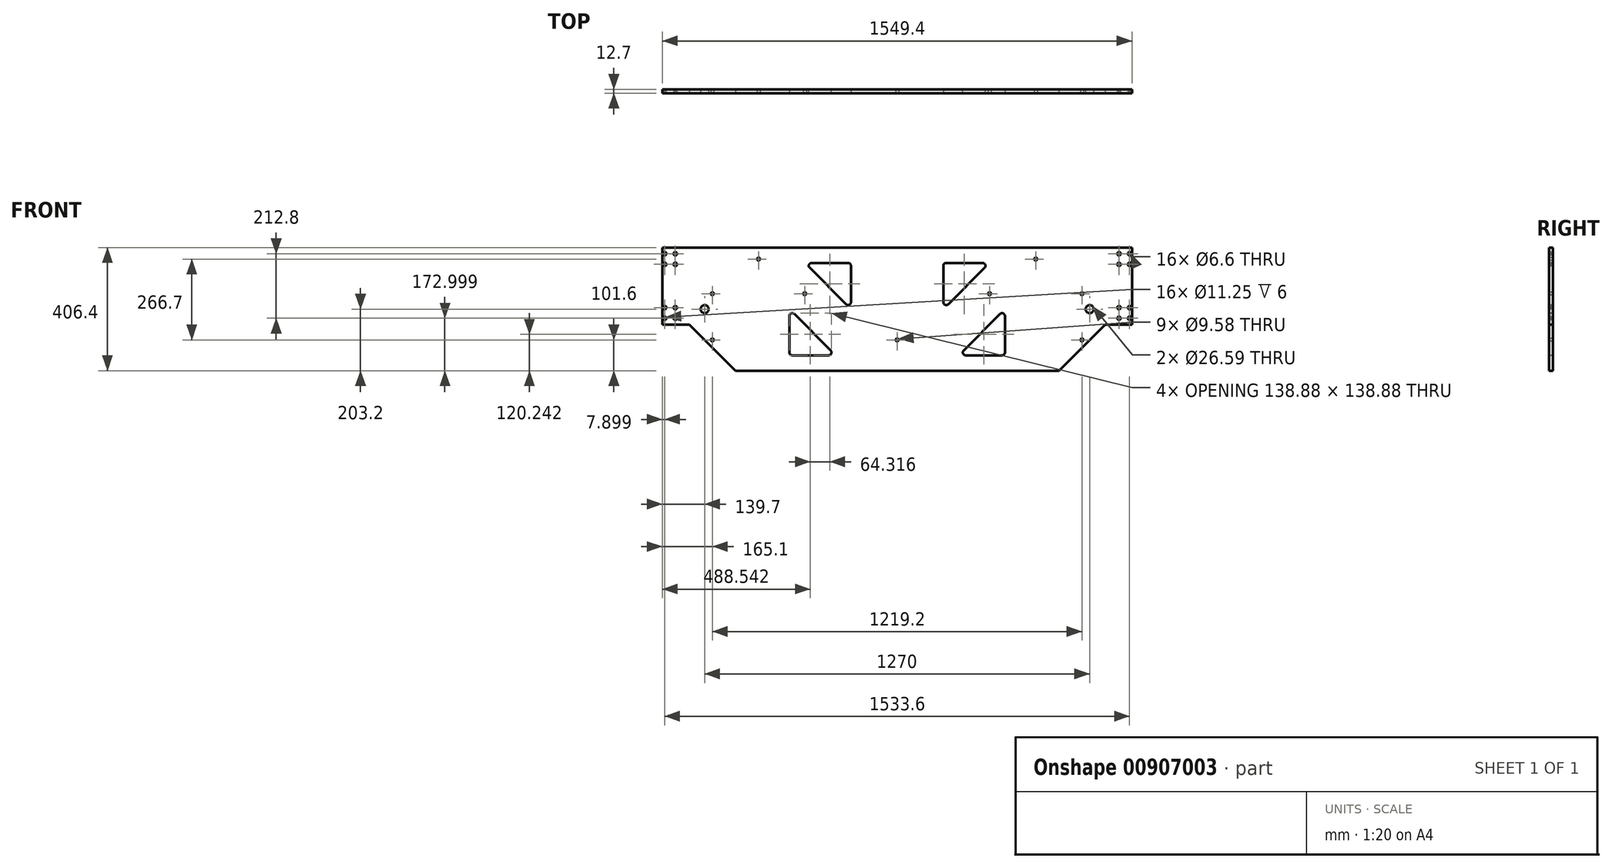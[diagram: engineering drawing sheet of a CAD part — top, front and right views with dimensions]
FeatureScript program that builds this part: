
annotation { "Feature Type Name" : "Feature", "Feature Type Description" : "" }
export const myFeature = defineFeature(function(context is Context, id is Id, definition is map)
    precondition{}
    {
        {
            var Q0;
            Q0=qCreatedBy(makeId("Front.planeOp"),FACE);
            var sketch = newSketch(context, id + "F0", { "sketchPlane" : qUnion([Q0])});
            skLineSegment(sketch, "E0.bottom", {"start": v(774.7, 127) * mm, "end": v(-774.7, 127) * mm});
            skLineSegment(sketch, "E0.top", {"start": v(774.7, -127) * mm, "end": v(-774.7, -127) * mm});
            skLineSegment(sketch, "E0.left", {"start": v(774.7, 127) * mm, "end": v(774.7, -127) * mm});
            skLineSegment(sketch, "E0.right", {"start": v(-774.7, 127) * mm, "end": v(-774.7, -127) * mm});
            skPoint(sketch, "E0.middle", {"position": v(0, 0) * mm});
            skSolve(sketch);
        }
        {
            var Q0;
            Q0=makeQuery(id+"F0.imprint","IMPRINT",FACE,{"disambiguationData":[TD([[makeQuery(id+"F0.imprint","IMPRINT",EDGE,{"derivedFrom":sQuery(id+"F0.wireOp",EDGE,"E0.bottom")}),1.0]])]});
            extrude(context, id + "F1", {"entities" : qUnion([Q0]), "depth" : 12.7 * mm, "offsetDistance" : 25.4 * mm});
        }
        {
            var Q0;
            Q0=makeQuery(id+"F1.opExtrude","CAP_FACE",FACE,{"disambiguationData":[OSD([sQuery(id+"F0.wireOp",EDGE,"E0.bottom"),sQuery(id+"F0.wireOp",EDGE,"E0.top"),sQuery(id+"F0.wireOp",EDGE,"E0.left"),sQuery(id+"F0.wireOp",EDGE,"E0.right")])],"isStart":false});
            var sketch = newSketch(context, id + "F2", { "sketchPlane" : qUnion([Q0])});
            skLineSegment(sketch, "E1.bottom", {"start": v(-766.8, 106.4) * mm, "end": v(-731.8, 106.4) * mm, "construction": true});
            skLineSegment(sketch, "E1.top", {"start": v(-766.8, 71.4) * mm, "end": v(-731.8, 71.4) * mm, "construction": true});
            skLineSegment(sketch, "E1.left", {"start": v(-766.8, 106.4) * mm, "end": v(-766.8, 71.4) * mm, "construction": true});
            skLineSegment(sketch, "E1.right", {"start": v(-731.8, 106.4) * mm, "end": v(-731.8, 71.4) * mm, "construction": true});
            skLineSegment(sketch, "E2.0.1.0", {"start": v(-766.8, -71.4) * mm, "end": v(-766.8, -106.4) * mm, "construction": true});
            skLineSegment(sketch, "E2.0.1.1", {"start": v(-766.8, -71.4) * mm, "end": v(-731.8, -71.4) * mm, "construction": true});
            skLineSegment(sketch, "E2.0.1.2", {"start": v(-766.8, -106.4) * mm, "end": v(-731.8, -106.4) * mm, "construction": true});
            skLineSegment(sketch, "E2.0.1.3", {"start": v(-731.8, -71.4) * mm, "end": v(-731.8, -106.4) * mm, "construction": true});
            skLineSegment(sketch, "E2.1.0.0", {"start": v(731.8, 106.4) * mm, "end": v(731.8, 71.4) * mm, "construction": true});
            skLineSegment(sketch, "E2.1.0.1", {"start": v(731.8, 106.4) * mm, "end": v(766.8, 106.4) * mm, "construction": true});
            skLineSegment(sketch, "E2.1.0.2", {"start": v(731.8, 71.4) * mm, "end": v(766.8, 71.4) * mm, "construction": true});
            skLineSegment(sketch, "E2.1.0.3", {"start": v(766.8, 106.4) * mm, "end": v(766.8, 71.4) * mm, "construction": true});
            skLineSegment(sketch, "E2.1.1.0", {"start": v(731.8, -71.4) * mm, "end": v(731.8, -106.4) * mm, "construction": true});
            skLineSegment(sketch, "E2.1.1.1", {"start": v(731.8, -71.4) * mm, "end": v(766.8, -71.4) * mm, "construction": true});
            skLineSegment(sketch, "E2.1.1.2", {"start": v(731.8, -106.4) * mm, "end": v(766.8, -106.4) * mm, "construction": true});
            skLineSegment(sketch, "E2.1.1.3", {"start": v(766.8, -71.4) * mm, "end": v(766.8, -106.4) * mm, "construction": true});
            skLineSegment(sketch, "E2.2.0.0", {"start": v(2230.4, 106.4) * mm, "end": v(2230.4, 71.4) * mm, "construction": true});
            skLineSegment(sketch, "E2.2.0.1", {"start": v(2230.4, 106.4) * mm, "end": v(2265.4, 106.4) * mm, "construction": true});
            skLineSegment(sketch, "E2.2.0.2", {"start": v(2230.4, 71.4) * mm, "end": v(2265.4, 71.4) * mm, "construction": true});
            skLineSegment(sketch, "E2.2.0.3", {"start": v(2265.4, 106.4) * mm, "end": v(2265.4, 71.4) * mm, "construction": true});
            skLineSegment(sketch, "E2.2.1.0", {"start": v(2230.4, -71.4) * mm, "end": v(2230.4, -106.4) * mm, "construction": true});
            skLineSegment(sketch, "E2.2.1.1", {"start": v(2230.4, -71.4) * mm, "end": v(2265.4, -71.4) * mm, "construction": true});
            skLineSegment(sketch, "E2.2.1.2", {"start": v(2230.4, -106.4) * mm, "end": v(2265.4, -106.4) * mm, "construction": true});
            skLineSegment(sketch, "E2.2.1.3", {"start": v(2265.4, -71.4) * mm, "end": v(2265.4, -106.4) * mm, "construction": true});
            skLineSegment(sketch, "E2.direction1", {"start": v(-766.8, 71.4) * mm, "end": v(731.8, 71.4) * mm, "construction": true});
            skLineSegment(sketch, "E2.direction2", {"start": v(-766.8, 71.4) * mm, "end": v(-766.8, -106.4) * mm, "construction": true});
            skSolve(sketch);
        }
        {
            var Q0;
            Q0=sQuery(id+"F2.wireOp",VERTEX,"E1.bottom.start");
            var Q1;
            Q1=sQuery(id+"F2.wireOp",VERTEX,"E1.bottom.end");
            var Q2;
            Q2=sQuery(id+"F2.wireOp",VERTEX,"E1.top.end");
            var Q3;
            Q3=sQuery(id+"F2.wireOp",VERTEX,"E1.top.start");
            var Q4;
            Q4=sQuery(id+"F2.wireOp",VERTEX,"E2.0.1.1.end");
            var Q5;
            Q5=sQuery(id+"F2.wireOp",VERTEX,"E2.0.1.0.start");
            var Q6;
            Q6=sQuery(id+"F2.wireOp",VERTEX,"E2.0.1.0.end");
            var Q7;
            Q7=sQuery(id+"F2.wireOp",VERTEX,"E2.0.1.2.end");
            var Q8;
            Q8=sQuery(id+"F2.wireOp",VERTEX,"E2.1.0.0.start");
            var Q9;
            Q9=sQuery(id+"F2.wireOp",VERTEX,"E2.1.0.1.end");
            var Q10;
            Q10=sQuery(id+"F2.wireOp",VERTEX,"E2.1.0.2.end");
            var Q11;
            Q11=sQuery(id+"F2.wireOp",VERTEX,"E2.1.0.0.end");
            var Q12;
            Q12=sQuery(id+"F2.wireOp",VERTEX,"E2.1.1.0.start");
            var Q13;
            Q13=sQuery(id+"F2.wireOp",VERTEX,"E2.1.1.1.end");
            var Q14;
            Q14=sQuery(id+"F2.wireOp",VERTEX,"E2.1.1.2.end");
            var Q15;
            Q15=sQuery(id+"F2.wireOp",VERTEX,"E2.1.1.0.end");
            var Q16;
            Q16=makeQuery(id+"F1.opExtrude","SWEPT_BODY",BODY,{"disambiguationData":[OSD([sQuery(id+"F0.wireOp",EDGE,"E0.bottom"),sQuery(id+"F0.wireOp",EDGE,"E0.top"),sQuery(id+"F0.wireOp",EDGE,"E0.left"),sQuery(id+"F0.wireOp",EDGE,"E0.right")])]});
            hole(context, id + "F3", {"style" : HoleStyle.C_BORE, "endStyle" : HoleEndStyle.THROUGH, "standardTappedOrClearance" : lookupTablePath({ "fit" : "Normal", "standard" : "ISO", "size" : "M6", "type" : "Clearance" }), "standardBlindInLast" : lookupTablePath({ "fit" : "Normal", "standard" : "ISO", "engagement" : "75%", "pitch" : "1 mm", "size" : "M6", "type" : "Clearance & tapped" }), "holeDiameter" : 6.6 * mm, "cBoreDiameter" : 11.25 * mm, "cBoreDepth" : 6 * mm, "majorDiameter" : 7.94 * mm, "isTappedThrough" : true, "tappedDepth" : 12.7 * mm, "tapClearance" : 3, "locations" : qUnion([Q0, Q1, Q2, Q3, Q4, Q5, Q6, Q7, Q8, Q9, Q10, Q11, Q12, Q13, Q14, Q15]), "scope" : qUnion([Q16])});
        }
        {
            var Q0;
            Q0=makeQuery(id+"F1.opExtrude","CAP_FACE",FACE,{"disambiguationData":[OSD([sQuery(id+"F0.wireOp",EDGE,"E0.bottom"),sQuery(id+"F0.wireOp",EDGE,"E0.top"),sQuery(id+"F0.wireOp",EDGE,"E0.left"),sQuery(id+"F0.wireOp",EDGE,"E0.right")])],"isStart":false});
            var sketch = newSketch(context, id + "F4", { "sketchPlane" : qUnion([Q0])});
            skLineSegment(sketch, "E3.bottom", {"start": v(-8.33, 2.77) * mm, "end": v(-15.95, 2.77) * mm});
            skLineSegment(sketch, "E3.top", {"start": v(-8.33, -2.77) * mm, "end": v(-15.95, -2.77) * mm});
            skLineSegment(sketch, "E3.left", {"start": v(-8.33, 2.77) * mm, "end": v(-8.33, -2.77) * mm});
            skLineSegment(sketch, "E3.right", {"start": v(-15.95, 2.77) * mm, "end": v(-15.95, -2.77) * mm});
            skArc(sketch, "E4", {"start": v(-15.95, 2.77) * mm, "mid": v(-18.72, 0) * mm, "end": v(-15.95, -2.77) * mm});
            skArc(sketch, "E5", {"start": v(-8.33, -2.77) * mm, "mid": v(-5.56, 0) * mm, "end": v(-8.33, 2.77) * mm});
            skArc(sketch, "E6.0.1.0", {"start": v(-8.33, -66.27) * mm, "mid": v(-5.56, -63.5) * mm, "end": v(-8.33, -60.73) * mm});
            skLineSegment(sketch, "E6.0.1.1", {"start": v(-15.95, -60.73) * mm, "end": v(-15.95, -66.27) * mm});
            skLineSegment(sketch, "E6.0.1.2", {"start": v(-8.33, -60.73) * mm, "end": v(-8.33, -66.27) * mm});
            skLineSegment(sketch, "E6.0.1.3", {"start": v(-8.33, -60.73) * mm, "end": v(-15.95, -60.73) * mm});
            skArc(sketch, "E6.0.1.4", {"start": v(-15.95, -60.73) * mm, "mid": v(-18.72, -63.5) * mm, "end": v(-15.95, -66.27) * mm});
            skLineSegment(sketch, "E6.0.1.5", {"start": v(-8.33, -66.27) * mm, "end": v(-15.95, -66.27) * mm});
            skArc(sketch, "E6.1.0.0", {"start": v(16.67, -2.77) * mm, "mid": v(19.44, 0) * mm, "end": v(16.67, 2.77) * mm});
            skLineSegment(sketch, "E6.1.0.1", {"start": v(9.05, 2.77) * mm, "end": v(9.05, -2.77) * mm});
            skLineSegment(sketch, "E6.1.0.2", {"start": v(16.67, 2.77) * mm, "end": v(16.67, -2.77) * mm});
            skLineSegment(sketch, "E6.1.0.3", {"start": v(16.67, 2.77) * mm, "end": v(9.05, 2.77) * mm});
            skArc(sketch, "E6.1.0.4", {"start": v(9.05, 2.77) * mm, "mid": v(6.28, 0) * mm, "end": v(9.05, -2.77) * mm});
            skLineSegment(sketch, "E6.1.0.5", {"start": v(16.67, -2.77) * mm, "end": v(9.05, -2.77) * mm});
            skArc(sketch, "E6.1.1.0", {"start": v(16.67, -66.27) * mm, "mid": v(19.44, -63.5) * mm, "end": v(16.67, -60.73) * mm});
            skLineSegment(sketch, "E6.1.1.1", {"start": v(9.05, -60.73) * mm, "end": v(9.05, -66.27) * mm});
            skLineSegment(sketch, "E6.1.1.2", {"start": v(16.67, -60.73) * mm, "end": v(16.67, -66.27) * mm});
            skLineSegment(sketch, "E6.1.1.3", {"start": v(16.67, -60.73) * mm, "end": v(9.05, -60.73) * mm});
            skArc(sketch, "E6.1.1.4", {"start": v(9.05, -60.73) * mm, "mid": v(6.28, -63.5) * mm, "end": v(9.05, -66.27) * mm});
            skLineSegment(sketch, "E6.1.1.5", {"start": v(16.67, -66.27) * mm, "end": v(9.05, -66.27) * mm});
            skLineSegment(sketch, "E6.direction1", {"start": v(-15.95, -2.77) * mm, "end": v(9.05, -2.77) * mm, "construction": true});
            skLineSegment(sketch, "E6.direction2", {"start": v(-15.95, -2.77) * mm, "end": v(-15.95, -66.27) * mm, "construction": true});
            skSolve(sketch);
        }
        {
            var Q0;
            Q0=makeQuery(id+"F1.opExtrude","CAP_FACE",FACE,{"disambiguationData":[OSD([sQuery(id+"F0.wireOp",EDGE,"E0.bottom"),sQuery(id+"F0.wireOp",EDGE,"E0.top"),sQuery(id+"F0.wireOp",EDGE,"E0.left"),sQuery(id+"F0.wireOp",EDGE,"E0.right")])],"isStart":false});
            var sketch = newSketch(context, id + "F5", { "sketchPlane" : qUnion([Q0])});
            skLineSegment(sketch, "E7", {"start": v(-685.8, -127) * mm, "end": v(685.8, -127) * mm});
            skLineSegment(sketch, "E8", {"start": v(685.8, -127) * mm, "end": v(533.4, -279.4) * mm});
            skLineSegment(sketch, "E9", {"start": v(533.4, -279.4) * mm, "end": v(-533.4, -279.4) * mm});
            skLineSegment(sketch, "E10", {"start": v(-533.4, -279.4) * mm, "end": v(-685.8, -127) * mm});
            skLineSegment(sketch, "E11", {"start": v(0, -127) * mm, "end": v(0, -279.4) * mm, "construction": true});
            skSolve(sketch);
        }
        {
            var Q0;
            Q0=makeQuery(id+"F4.imprint","IMPRINT",FACE,{"disambiguationData":[TD([[makeQuery(id+"F4.imprint","IMPRINT",EDGE,{"derivedFrom":sQuery(id+"F4.wireOp",EDGE,"E3.bottom")}),1.0]])]});
            var Q1;
            Q1=makeQuery(id+"F4.imprint","IMPRINT",FACE,{"disambiguationData":[TD([[makeQuery(id+"F4.imprint","IMPRINT",EDGE,{"derivedFrom":sQuery(id+"F4.wireOp",EDGE,"E3.right")}),-1.0]])]});
            var Q2;
            Q2=makeQuery(id+"F4.imprint","IMPRINT",FACE,{"disambiguationData":[TD([[makeQuery(id+"F4.imprint","IMPRINT",EDGE,{"derivedFrom":sQuery(id+"F4.wireOp",EDGE,"E3.left")}),1.0]])]});
            var Q3;
            Q3=makeQuery(id+"F4.imprint","IMPRINT",FACE,{"disambiguationData":[TD([[makeQuery(id+"F4.imprint","IMPRINT",EDGE,{"derivedFrom":sQuery(id+"F4.wireOp",EDGE,"E6.1.0.1")}),1.0]])]});
            var Q4;
            Q4=makeQuery(id+"F4.imprint","IMPRINT",FACE,{"disambiguationData":[TD([[makeQuery(id+"F4.imprint","IMPRINT",EDGE,{"derivedFrom":sQuery(id+"F4.wireOp",EDGE,"E6.1.0.1")}),-1.0]])]});
            var Q5;
            Q5=makeQuery(id+"F4.imprint","IMPRINT",FACE,{"disambiguationData":[TD([[makeQuery(id+"F4.imprint","IMPRINT",EDGE,{"derivedFrom":sQuery(id+"F4.wireOp",EDGE,"E6.1.0.0")}),1.0]])]});
            var Q6;
            Q6=makeQuery(id+"F4.imprint","IMPRINT",FACE,{"disambiguationData":[TD([[makeQuery(id+"F4.imprint","IMPRINT",EDGE,{"derivedFrom":sQuery(id+"F4.wireOp",EDGE,"E6.1.1.0")}),1.0]])]});
            var Q7;
            Q7=makeQuery(id+"F4.imprint","IMPRINT",FACE,{"disambiguationData":[TD([[makeQuery(id+"F4.imprint","IMPRINT",EDGE,{"derivedFrom":sQuery(id+"F4.wireOp",EDGE,"E6.1.1.1")}),1.0]])]});
            var Q8;
            Q8=makeQuery(id+"F4.imprint","IMPRINT",FACE,{"disambiguationData":[TD([[makeQuery(id+"F4.imprint","IMPRINT",EDGE,{"derivedFrom":sQuery(id+"F4.wireOp",EDGE,"E6.1.1.1")}),-1.0]])]});
            var Q9;
            Q9=makeQuery(id+"F4.imprint","IMPRINT",FACE,{"disambiguationData":[TD([[makeQuery(id+"F4.imprint","IMPRINT",EDGE,{"derivedFrom":sQuery(id+"F4.wireOp",EDGE,"E6.0.1.0")}),1.0]])]});
            var Q10;
            Q10=makeQuery(id+"F4.imprint","IMPRINT",FACE,{"disambiguationData":[TD([[makeQuery(id+"F4.imprint","IMPRINT",EDGE,{"derivedFrom":sQuery(id+"F4.wireOp",EDGE,"E6.0.1.1")}),1.0]])]});
            var Q11;
            Q11=makeQuery(id+"F4.imprint","IMPRINT",FACE,{"disambiguationData":[TD([[makeQuery(id+"F4.imprint","IMPRINT",EDGE,{"derivedFrom":sQuery(id+"F4.wireOp",EDGE,"E6.0.1.1")}),-1.0]])]});
            var Q12;
            Q12=makeQuery(id+"F5.imprint","IMPRINT",FACE,{"disambiguationData":[TD([[makeQuery(id+"F5.imprint","IMPRINT",EDGE,{"derivedFrom":sQuery(id+"F5.wireOp",EDGE,"E7")}),1.0]])]});
            extrude(context, id + "F6", {"entities" : qUnion([Q0, Q1, Q2, Q3, Q4, Q5, Q6, Q7, Q8, Q9, Q10, Q11, Q12]), "operationType" : NewBodyOperationType.ADD, "oppositeDirection" : true, "depth" : 12.7 * mm, "offsetDistance" : 25.4 * mm});
        }
        {
            var Q0;
            Q0=makeQuery(id+"F6.boolean.opBoolean","MERGE",FACE,{"derivedFrom":[makeQuery(id+"F1.opExtrude","CAP_FACE",FACE,{"disambiguationData":[OSD([sQuery(id+"F0.wireOp",EDGE,"E0.bottom"),sQuery(id+"F0.wireOp",EDGE,"E0.top"),sQuery(id+"F0.wireOp",EDGE,"E0.left"),sQuery(id+"F0.wireOp",EDGE,"E0.right")])],"isStart":false}),makeQuery(id+"F6.opExtrude","CAP_FACE",FACE,{"disambiguationData":[OSD([sQuery(id+"F5.wireOp",EDGE,"E7"),sQuery(id+"F5.wireOp",EDGE,"E8"),sQuery(id+"F5.wireOp",EDGE,"E9"),sQuery(id+"F5.wireOp",EDGE,"E10")])],"isStart":true})]});
            var sketch = newSketch(context, id + "F7", { "sketchPlane" : qUnion([Q0])});
            skLineSegment(sketch, "E12", {"start": v(-635, -76.2) * mm, "end": v(635, -76.2) * mm, "construction": true});
            skLineSegment(sketch, "E13", {"start": v(0, 127) * mm, "end": v(0, -76.2) * mm, "construction": true});
            skSolve(sketch);
        }
        {
            var Q0;
            Q0=sQuery(id+"F7.wireOp",VERTEX,"E12.start");
            var Q1;
            Q1=sQuery(id+"F7.wireOp",VERTEX,"E12.end");
            var Q2;
            Q2=makeQuery(id+"F1.opExtrude","SWEPT_BODY",BODY,{"disambiguationData":[OSD([sQuery(id+"F0.wireOp",EDGE,"E0.bottom"),sQuery(id+"F0.wireOp",EDGE,"E0.top"),sQuery(id+"F0.wireOp",EDGE,"E0.left"),sQuery(id+"F0.wireOp",EDGE,"E0.right")])]});
            hole(context, id + "F8", {"style" : HoleStyle.SIMPLE, "endStyle" : HoleEndStyle.THROUGH, "standardTappedOrClearance" : lookupTablePath({ "standard" : "ANSI", "engagement" : "75%", "pitch" : "12 tpi", "size" : "1 1/8", "type" : "Tapped" }), "standardBlindInLast" : lookupTablePath({ "standard" : "ANSI", "fit" : "Free", "engagement" : "75%", "pitch" : "12 tpi", "size" : "1 1/8", "type" : "Clearance & tapped" }), "holeDiameter" : 26.6 * mm, "majorDiameter" : 28.57 * mm, "showTappedDepth" : true, "isTappedThrough" : true, "tappedDepth" : 12.7 * mm, "tapClearance" : 3, "locations" : qUnion([Q0, Q1]), "scope" : qUnion([Q2])});
        }
        {
            var Q0;
            Q0=makeQuery(id+"F6.boolean.opBoolean","MERGE",FACE,{"derivedFrom":[makeQuery(id+"F1.opExtrude","CAP_FACE",FACE,{"disambiguationData":[OSD([sQuery(id+"F0.wireOp",EDGE,"E0.bottom"),sQuery(id+"F0.wireOp",EDGE,"E0.top"),sQuery(id+"F0.wireOp",EDGE,"E0.left"),sQuery(id+"F0.wireOp",EDGE,"E0.right")])],"isStart":false}),makeQuery(id+"F6.opExtrude","CAP_FACE",FACE,{"disambiguationData":[OSD([sQuery(id+"F5.wireOp",EDGE,"E7"),sQuery(id+"F5.wireOp",EDGE,"E8"),sQuery(id+"F5.wireOp",EDGE,"E9"),sQuery(id+"F5.wireOp",EDGE,"E10")])],"isStart":true})]});
            var sketch = newSketch(context, id + "F9", { "sketchPlane" : qUnion([Q0])});
            skLineSegment(sketch, "E14", {"start": v(-457.2, 88.9) * mm, "end": v(457.2, 88.9) * mm, "construction": true});
            skLineSegment(sketch, "E15", {"start": v(0, 0) * mm, "end": v(0, 88.9) * mm, "construction": true});
            skLineSegment(sketch, "E16", {"start": v(-609.6, -25.4) * mm, "end": v(609.6, -25.4) * mm, "construction": true});
            skLineSegment(sketch, "E17", {"start": v(0, 0) * mm, "end": v(0, -25.4) * mm, "construction": true});
            skLineSegment(sketch, "E18", {"start": v(-609.6, -177.8) * mm, "end": v(609.6, -177.8) * mm, "construction": true});
            skLineSegment(sketch, "E19", {"start": v(0, -25.4) * mm, "end": v(0, -177.8) * mm, "construction": true});
            skPoint(sketch, "E20", {"position": v(-304.8, -25.4) * mm});
            skPoint(sketch, "E21", {"position": v(304.8, -25.4) * mm});
            skSolve(sketch);
        }
        {
            var Q0;
            Q0=sQuery(id+"F9.wireOp",VERTEX,"E16.start");
            var Q1;
            Q1=sQuery(id+"F9.wireOp",VERTEX,"E18.start");
            var Q2;
            Q2=sQuery(id+"F9.wireOp",VERTEX,"E14.start");
            var Q3;
            Q3=sQuery(id+"F9.wireOp",VERTEX,"E14.end");
            var Q4;
            Q4=sQuery(id+"F9.wireOp",VERTEX,"E16.end");
            var Q5;
            Q5=sQuery(id+"F9.wireOp",VERTEX,"E18.end");
            var Q6;
            Q6=sQuery(id+"F9.wireOp",VERTEX,"E20");
            var Q7;
            Q7=sQuery(id+"F9.wireOp",VERTEX,"E21");
            var Q8;
            Q8=sQuery(id+"F9.wireOp",VERTEX,"E19.end");
            var Q9;
            Q9=makeQuery(id+"F1.opExtrude","SWEPT_BODY",BODY,{"disambiguationData":[OSD([sQuery(id+"F0.wireOp",EDGE,"E0.bottom"),sQuery(id+"F0.wireOp",EDGE,"E0.top"),sQuery(id+"F0.wireOp",EDGE,"E0.left"),sQuery(id+"F0.wireOp",EDGE,"E0.right")])]});
            hole(context, id + "F10", {"style" : HoleStyle.SIMPLE, "endStyle" : HoleEndStyle.THROUGH, "standardTappedOrClearance" : lookupTablePath({ "standard" : "ANSI", "size" : "V (0.38)", "type" : "Drilled" }), "standardBlindInLast" : lookupTablePath({ "standard" : "ANSI", "size" : "V (0.38)", "type" : "Drilled" }), "holeDiameter" : 9.58 * mm, "majorDiameter" : 28.57 * mm, "isTappedThrough" : true, "tappedDepth" : 12.7 * mm, "tapClearance" : 3, "locations" : qUnion([Q0, Q1, Q2, Q3, Q4, Q5, Q6, Q7, Q8]), "scope" : qUnion([Q9])});
        }
        {
            var Q0;
            Q0=makeQuery(id+"F6.boolean.opBoolean","MERGE",FACE,{"derivedFrom":[makeQuery(id+"F1.opExtrude","CAP_FACE",FACE,{"disambiguationData":[OSD([sQuery(id+"F0.wireOp",EDGE,"E0.bottom"),sQuery(id+"F0.wireOp",EDGE,"E0.top"),sQuery(id+"F0.wireOp",EDGE,"E0.left"),sQuery(id+"F0.wireOp",EDGE,"E0.right")])],"isStart":false}),makeQuery(id+"F6.opExtrude","CAP_FACE",FACE,{"disambiguationData":[OSD([sQuery(id+"F5.wireOp",EDGE,"E7"),sQuery(id+"F5.wireOp",EDGE,"E8"),sQuery(id+"F5.wireOp",EDGE,"E9"),sQuery(id+"F5.wireOp",EDGE,"E10")])],"isStart":true})]});
            var sketch = newSketch(context, id + "F11", { "sketchPlane" : qUnion([Q0])});
            skLineSegment(sketch, "E22", {"start": v(-355.6, -76.2) * mm, "end": v(-355.6, -228.6) * mm});
            skLineSegment(sketch, "E23", {"start": v(-355.6, -228.6) * mm, "end": v(-203.2, -228.6) * mm});
            skLineSegment(sketch, "E24", {"start": v(-203.2, -228.6) * mm, "end": v(-355.6, -76.2) * mm});
            skLineSegment(sketch, "E25", {"start": v(-304.8, 76.2) * mm, "end": v(-152.4, 76.2) * mm});
            skLineSegment(sketch, "E26", {"start": v(-152.4, 76.2) * mm, "end": v(-152.4, -76.2) * mm});
            skLineSegment(sketch, "E27", {"start": v(-152.4, -76.2) * mm, "end": v(-304.8, 76.2) * mm});
            skLineSegment(sketch, "E28", {"start": v(0, 0) * mm, "end": v(0, 171.18) * mm});
            skPoint(sketch, "E28.endSnap0", {"position": v(0, 127) * mm});
            skLineSegment(sketch, "E29.MirrorCS", {"start": v(304.8, 76.2) * mm, "end": v(152.4, 76.2) * mm});
            skLineSegment(sketch, "E30.MirrorCS", {"start": v(152.4, 76.2) * mm, "end": v(152.4, -76.2) * mm});
            skLineSegment(sketch, "E31.MirrorCS", {"start": v(152.4, -76.2) * mm, "end": v(304.8, 76.2) * mm});
            skLineSegment(sketch, "E32.MirrorCS", {"start": v(203.2, -228.6) * mm, "end": v(355.6, -76.2) * mm});
            skLineSegment(sketch, "E33.MirrorCS", {"start": v(355.6, -76.2) * mm, "end": v(355.6, -228.6) * mm});
            skLineSegment(sketch, "E34.MirrorCS", {"start": v(355.6, -228.6) * mm, "end": v(203.2, -228.6) * mm});
            skSolve(sketch);
        }
        {
            var Q0;
            Q0=makeQuery(id+"F11.imprint","IMPRINT",FACE,{"disambiguationData":[TD([[makeQuery(id+"F11.imprint","IMPRINT",EDGE,{"derivedFrom":sQuery(id+"F11.wireOp",EDGE,"E25")}),-1.0]])]});
            var Q1;
            Q1=makeQuery(id+"F11.imprint","IMPRINT",FACE,{"disambiguationData":[TD([[makeQuery(id+"F11.imprint","IMPRINT",EDGE,{"derivedFrom":sQuery(id+"F11.wireOp",EDGE,"E29.MirrorCS")}),1.0]])]});
            var Q2;
            Q2=makeQuery(id+"F11.imprint","IMPRINT",FACE,{"disambiguationData":[TD([[makeQuery(id+"F11.imprint","IMPRINT",EDGE,{"derivedFrom":sQuery(id+"F11.wireOp",EDGE,"E32.MirrorCS")}),-1.0]])]});
            var Q3;
            Q3=makeQuery(id+"F11.imprint","IMPRINT",FACE,{"disambiguationData":[TD([[makeQuery(id+"F11.imprint","IMPRINT",EDGE,{"derivedFrom":sQuery(id+"F11.wireOp",EDGE,"E22")}),1.0]])]});
            extrude(context, id + "F12", {"entities" : qUnion([Q0, Q1, Q2, Q3]), "operationType" : NewBodyOperationType.REMOVE, "oppositeDirection" : true, "depth" : 25.4 * mm, "offsetDistance" : 25.4 * mm});
        }
        {
            var Q0;
            Q0=makeQuery(id+"F12.boolean.opBoolean","COPY",EDGE,{"derivedFrom":makeQuery(id+"F12.opExtrude","SWEPT_EDGE",EDGE,{"disambiguationData":[OSD([sQuery(id+"F11.wireOp",EDGE,"E25"),sQuery(id+"F11.wireOp",EDGE,"E27")])]})});
            var Q1;
            Q1=makeQuery(id+"F12.boolean.opBoolean","COPY",EDGE,{"derivedFrom":makeQuery(id+"F12.opExtrude","SWEPT_EDGE",EDGE,{"disambiguationData":[OSD([sQuery(id+"F11.wireOp",EDGE,"E25"),sQuery(id+"F11.wireOp",EDGE,"E26")])]})});
            var Q2;
            Q2=makeQuery(id+"F12.boolean.opBoolean","COPY",EDGE,{"derivedFrom":makeQuery(id+"F12.opExtrude","SWEPT_EDGE",EDGE,{"disambiguationData":[OSD([sQuery(id+"F11.wireOp",EDGE,"E22"),sQuery(id+"F11.wireOp",EDGE,"E24")])]})});
            var Q3;
            Q3=makeQuery(id+"F12.boolean.opBoolean","COPY",EDGE,{"derivedFrom":makeQuery(id+"F12.opExtrude","SWEPT_EDGE",EDGE,{"disambiguationData":[OSD([sQuery(id+"F11.wireOp",EDGE,"E26"),sQuery(id+"F11.wireOp",EDGE,"E27")])]})});
            var Q4;
            Q4=makeQuery(id+"F12.boolean.opBoolean","COPY",EDGE,{"derivedFrom":makeQuery(id+"F12.opExtrude","SWEPT_EDGE",EDGE,{"disambiguationData":[OSD([sQuery(id+"F11.wireOp",EDGE,"E22"),sQuery(id+"F11.wireOp",EDGE,"E23")])]})});
            var Q5;
            Q5=makeQuery(id+"F12.boolean.opBoolean","COPY",EDGE,{"derivedFrom":makeQuery(id+"F12.opExtrude","SWEPT_EDGE",EDGE,{"disambiguationData":[OSD([sQuery(id+"F11.wireOp",EDGE,"E23"),sQuery(id+"F11.wireOp",EDGE,"E24")])]})});
            var Q6;
            Q6=makeQuery(id+"F12.boolean.opBoolean","COPY",EDGE,{"derivedFrom":makeQuery(id+"F12.opExtrude","SWEPT_EDGE",EDGE,{"disambiguationData":[OSD([sQuery(id+"F11.wireOp",EDGE,"E33.MirrorCS"),sQuery(id+"F11.wireOp",EDGE,"E34.MirrorCS")])]})});
            var Q7;
            Q7=makeQuery(id+"F12.boolean.opBoolean","COPY",EDGE,{"derivedFrom":makeQuery(id+"F12.opExtrude","SWEPT_EDGE",EDGE,{"disambiguationData":[OSD([sQuery(id+"F11.wireOp",EDGE,"E29.MirrorCS"),sQuery(id+"F11.wireOp",EDGE,"E30.MirrorCS")])]})});
            var Q8;
            Q8=makeQuery(id+"F12.boolean.opBoolean","COPY",EDGE,{"derivedFrom":makeQuery(id+"F12.opExtrude","SWEPT_EDGE",EDGE,{"disambiguationData":[OSD([sQuery(id+"F11.wireOp",EDGE,"E30.MirrorCS"),sQuery(id+"F11.wireOp",EDGE,"E31.MirrorCS")])]})});
            var Q9;
            Q9=makeQuery(id+"F12.boolean.opBoolean","COPY",EDGE,{"derivedFrom":makeQuery(id+"F12.opExtrude","SWEPT_EDGE",EDGE,{"disambiguationData":[OSD([sQuery(id+"F11.wireOp",EDGE,"E32.MirrorCS"),sQuery(id+"F11.wireOp",EDGE,"E34.MirrorCS")])]})});
            var Q10;
            Q10=makeQuery(id+"F12.boolean.opBoolean","COPY",EDGE,{"derivedFrom":makeQuery(id+"F12.opExtrude","SWEPT_EDGE",EDGE,{"disambiguationData":[OSD([sQuery(id+"F11.wireOp",EDGE,"E29.MirrorCS"),sQuery(id+"F11.wireOp",EDGE,"E31.MirrorCS")])]})});
            var Q11;
            Q11=makeQuery(id+"F12.boolean.opBoolean","COPY",EDGE,{"derivedFrom":makeQuery(id+"F12.opExtrude","SWEPT_EDGE",EDGE,{"disambiguationData":[OSD([sQuery(id+"F11.wireOp",EDGE,"E32.MirrorCS"),sQuery(id+"F11.wireOp",EDGE,"E33.MirrorCS")])]})});
            fillet(context, id + "F13", {"entities" : qUnion([Q0, Q1, Q2, Q3, Q4, Q5, Q6, Q7, Q8, Q9, Q10, Q11]), "tangentPropagation" : true, "radius" : 9.52 * mm, "defaultsChanged" : false, "vertexSettings" : [], "allowEdgeOverflow" : false});
        }
    });
